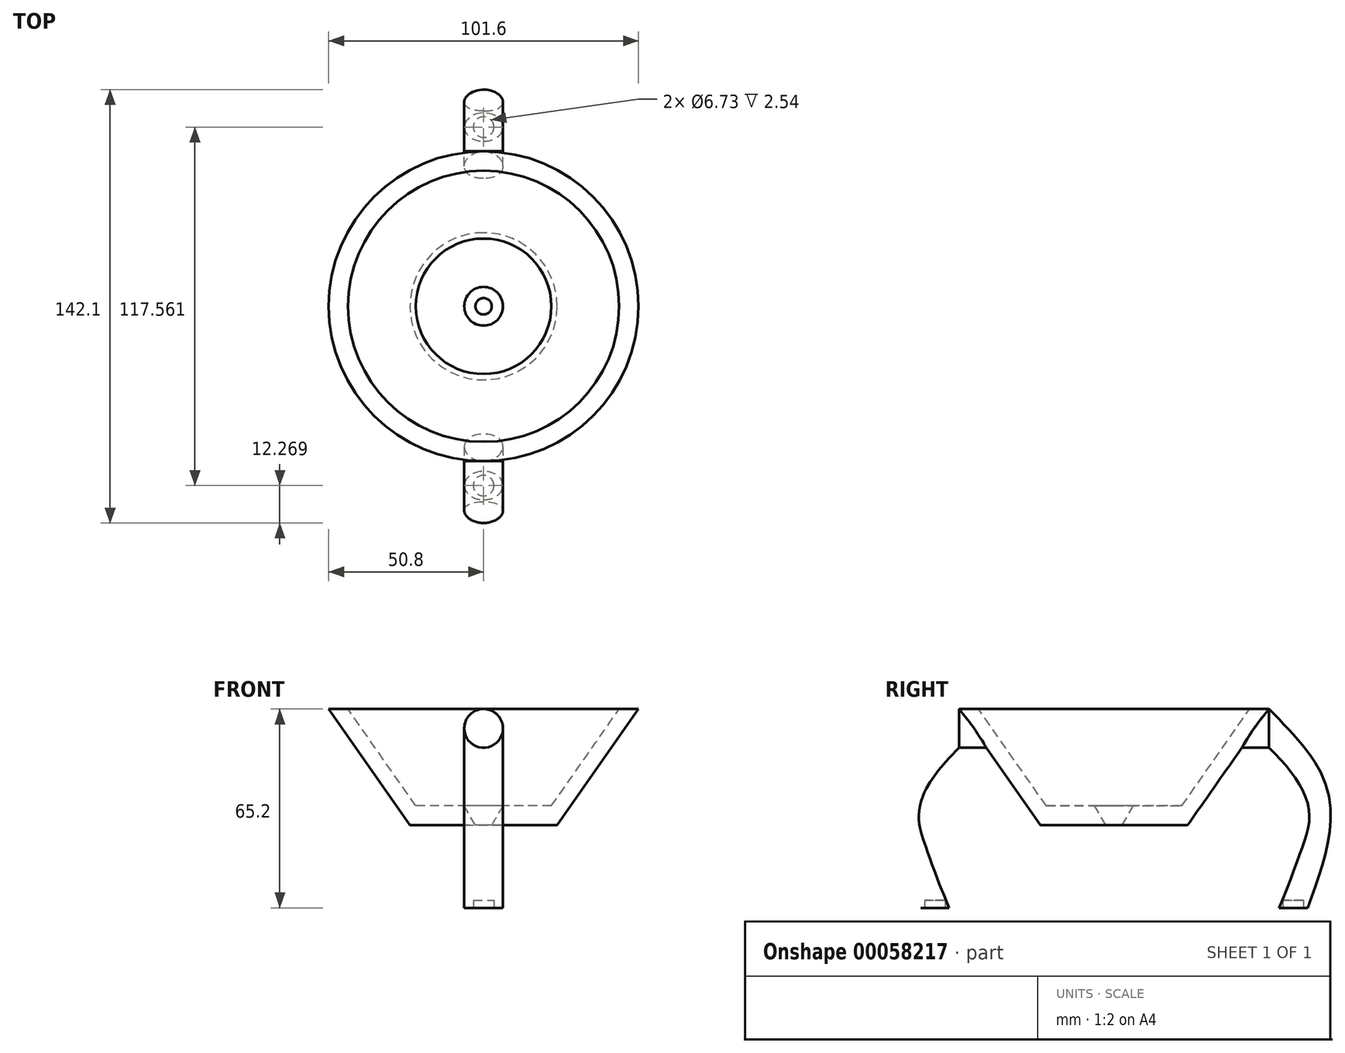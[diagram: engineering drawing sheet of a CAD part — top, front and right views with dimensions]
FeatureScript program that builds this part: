
annotation { "Feature Type Name" : "Feature", "Feature Type Description" : "" }
export const myFeature = defineFeature(function(context is Context, id is Id, definition is map)
    precondition{}
    {
        {
            var Q0;
            Q0=qCreatedBy(makeId("Top.planeOp"),FACE);
            var sketch = newSketch(context, id + "F0", { "sketchPlane" : qUnion([Q0])});
            skCircle(sketch, "E0", {"center": v(0, 0) * mm, "radius": 50.8 * mm});
            skSolve(sketch);
        }
        {
            var Q0;
            Q0 = qSketchRegion(id + "F0", true);
            extrude(context, id + "F1", {"entities" : qUnion([Q0]), "oppositeDirection" : true, "depth" : 38.1 * mm, "hasDraft" : true, "draftAngle" : 35 * degree, "draftPullDirection" : true});
        }
        {
            var Q0;
            Q0=makeQuery(id+"F1.opExtrude","CAP_FACE",FACE,{"disambiguationData":[OSD([sQuery(id+"F0.wireOp",EDGE,"E0")])],"isStart":true});
            var sketch = newSketch(context, id + "F2", { "sketchPlane" : qUnion([Q0])});
            skCircle(sketch, "E1", {"center": v(0, 0) * mm, "radius": 44.45 * mm});
            skSolve(sketch);
        }
        {
            var Q0;
            Q0 = qSketchRegion(id + "F2", true);
            extrude(context, id + "F3", {"entities" : qUnion([Q0]), "operationType" : NewBodyOperationType.REMOVE, "oppositeDirection" : true, "depth" : 31.75 * mm, "hasDraft" : true, "draftAngle" : 35 * degree, "draftPullDirection" : true});
        }
        {
            var Q0;
            Q0=qCreatedBy(makeId("Right.planeOp"),FACE);
            var sketch = newSketch(context, id + "F4", { "sketchPlane" : qUnion([Q0])});
            skPoint(sketch, "E2", {"position": v(-50.8, 0) * mm});
            skFitSpline(sketch, "E3", {"points": [v(-50.8, 0) * mm, v(-70.84, -31.02) * mm, v(-50.8, -97.59) * mm], "startDerivative": vector(-62.24, -64.04) * mm, "endDerivative": vector(44.05, -127.52) * mm});
            skFitSpline(sketch, "E4.MirrorCS", {"points": [v(50.8, 0) * mm, v(70.84, -31.02) * mm, v(50.8, -97.59) * mm], "startDerivative": vector(62.24, -64.04) * mm, "endDerivative": vector(-44.05, -127.52) * mm});
            skSolve(sketch);
        }
        {
            var Q0;
            Q0=sQuery(id+"F4.wireOp",VERTEX,"E2");
            var Q1;
            Q1=qCreatedBy(makeId("Front.planeOp"),FACE);
            cPlane(context, id + "F5", {"entities" : qUnion([Q0, Q1]), "cplaneType" : CPlaneType.PLANE_POINT, "offset" : 152.4 * mm, "width" : 152.4 * mm, "height" : 152.4 * mm});
        }
        {
            var Q0;
            Q0=qCreatedBy(id+"F5.planeOp",FACE);
            var sketch = newSketch(context, id + "F6", { "sketchPlane" : qUnion([Q0])});
            skCircle(sketch, "E5", {"center": v(0, -6.35) * mm, "radius": 6.35 * mm});
            skSolve(sketch);
        }
        {
            var Q0;
            Q0=makeQuery(id+"F6.imprint","IMPRINT",FACE,{"disambiguationData":[TD([[makeQuery(id+"F6.imprint","IMPRINT",EDGE,{"derivedFrom":sQuery(id+"F6.wireOp",EDGE,"E5")}),1.0]])]});
            var Q1;
            Q1=sQuery(id+"F4.wireOp",EDGE,"E3");
            sweep(context, id + "F7", {"profiles" : qUnion([Q0]), "path" : qUnion([Q1])});
        }
        {
            var Q0;
            Q0=makeQuery(id+"F6.imprint","IMPRINT",FACE,{"disambiguationData":[TD([[makeQuery(id+"F6.imprint","IMPRINT",EDGE,{"derivedFrom":sQuery(id+"F6.wireOp",EDGE,"E5")}),1.0]])]});
            var Q1;
            Q1=makeQuery(id+"F1.opExtrude","SWEPT_FACE",FACE,{"disambiguationData":[OSD([sQuery(id+"F0.wireOp",EDGE,"E0")])]});
            extrude(context, id + "F8", {"entities" : qUnion([Q0]), "endBound" : BoundingType.UP_TO_SURFACE, "oppositeDirection" : true, "endBoundEntityFace" : qUnion([Q1]), "depth" : 25.4 * mm});
        }
        {
            var Q0;
            Q0=makeQuery(id+"F7.opSweep","SWEPT_BODY",BODY,{"disambiguationData":[OSD([sQuery(id+"F4.wireOp",EDGE,"E3"),sQuery(id+"F6.wireOp",EDGE,"E5")])]});
            var Q1;
            Q1=makeQuery(id+"F8.opExtrude","SWEPT_BODY",BODY,{"disambiguationData":[OSD([sQuery(id+"F6.wireOp",EDGE,"E5")])]});
            var Q2;
            Q2=qCreatedBy(makeId("Front.planeOp"),FACE);
            mirror(context, id + "F9", {"operationType" : NewBodyOperationType.ADD, "entities" : qUnion([Q0, Q1]), "mirrorPlane" : qUnion([Q2])});
        }
        {
            var Q0;
            Q0=qCreatedBy(makeId("Right.planeOp"),FACE);
            var sketch = newSketch(context, id + "F10", { "sketchPlane" : qUnion([Q0])});
            skLineSegment(sketch, "E6", {"start": v(0, 0) * mm, "end": v(0, -8.97) * mm});
            skSolve(sketch);
        }
        {
            var Q0;
            Q0=makeQuery(id+"F7.opSweep","CAP_FACE",FACE,{"disambiguationData":[OSD([sQuery(id+"F4.wireOp",VERTEX,"E3.end"),sQuery(id+"F6.wireOp",EDGE,"E5")])],"isStart":false});
            var sketch = newSketch(context, id + "F11", { "sketchPlane" : qUnion([Q0])});
            skPoint(sketch, "E7", {"position": v(0, -11.28) * mm});
            skSolve(sketch);
        }
        {
            var Q0;
            Q0=sQuery(id+"F11.wireOp",VERTEX,"E7");
            var Q1;
            Q1=qCreatedBy(makeId("Top.planeOp"),FACE);
            cPlane(context, id + "F12", {"entities" : qUnion([Q0, Q1]), "cplaneType" : CPlaneType.PLANE_POINT, "offset" : 152.4 * mm, "width" : 152.4 * mm, "height" : 152.4 * mm});
        }
        {
            var Q0;
            Q0=qCreatedBy(id+"F12.planeOp",FACE);
            var sketch = newSketch(context, id + "F13", { "sketchPlane" : qUnion([Q0])});
            skLineSegment(sketch, "E8.bottom", {"start": v(-17.67, -100.3) * mm, "end": v(22.41, -100.3) * mm});
            skLineSegment(sketch, "E8.top", {"start": v(-17.67, 121.35) * mm, "end": v(22.41, 121.35) * mm});
            skLineSegment(sketch, "E8.left", {"start": v(-17.67, -100.3) * mm, "end": v(-17.67, 121.35) * mm});
            skLineSegment(sketch, "E8.right", {"start": v(22.41, -100.3) * mm, "end": v(22.41, 121.35) * mm});
            skSolve(sketch);
        }
        {
            var Q0;
            Q0 = qSketchRegion(id + "F13", true);
            extrude(context, id + "F14", {"entities" : qUnion([Q0]), "operationType" : NewBodyOperationType.REMOVE, "depth" : 38.1 * mm});
        }
        {
            var Q0;
            Q0=makeQuery(id+"F14.boolean.opBoolean","COPY",FACE,{"disambiguationData":[TD([makeQuery(id+"F7.opSweep","SWEPT_FACE",FACE,{"disambiguationData":[OSD([sQuery(id+"F4.wireOp",EDGE,"E3"),sQuery(id+"F6.wireOp",EDGE,"E5")])]})])],"derivedFrom":makeQuery(id+"F14.opExtrude","CAP_FACE",FACE,{"disambiguationData":[OSD([sQuery(id+"F13.wireOp",EDGE,"E8.bottom"),sQuery(id+"F13.wireOp",EDGE,"E8.top"),sQuery(id+"F13.wireOp",EDGE,"E8.left"),sQuery(id+"F13.wireOp",EDGE,"E8.right")])],"isStart":false})});
            var sketch = newSketch(context, id + "F15", { "sketchPlane" : qUnion([Q0])});
            skPoint(sketch, "E9", {"position": v(0, 63.44) * mm});
            skSolve(sketch);
        }
        {
            var Q0;
            Q0=makeQuery(id+"F14.boolean.opBoolean","COPY",FACE,{"disambiguationData":[TD([makeQuery(id+"F9.opPattern","COPY",FACE,{"derivedFrom":makeQuery(id+"F7.opSweep","SWEPT_FACE",FACE,{"disambiguationData":[OSD([sQuery(id+"F4.wireOp",EDGE,"E3"),sQuery(id+"F6.wireOp",EDGE,"E5")])]}),"instanceName":"1"})])],"derivedFrom":makeQuery(id+"F14.opExtrude","CAP_FACE",FACE,{"disambiguationData":[OSD([sQuery(id+"F13.wireOp",EDGE,"E8.bottom"),sQuery(id+"F13.wireOp",EDGE,"E8.top"),sQuery(id+"F13.wireOp",EDGE,"E8.left"),sQuery(id+"F13.wireOp",EDGE,"E8.right")])],"isStart":false})});
            var sketch = newSketch(context, id + "F16", { "sketchPlane" : qUnion([Q0])});
            skCircle(sketch, "E10", {"center": v(0, 0) * mm, "radius": 63.44 * mm});
            skSolve(sketch);
        }
        {
            var Q0;
            Q0 = qSketchRegion(id + "F16", true);
            extrude(context, id + "F17", {"entities" : qUnion([Q0]), "operationType" : NewBodyOperationType.ADD, "depth" : 6.35 * mm, "hasDraft" : true, "draftAngle" : 45 * degree, "draftPullDirection" : true});
        }
        {
            var Q0;
            Q0=makeQuery(id+"F17.opExtrude","CAP_FACE",FACE,{"disambiguationData":[OSD([sQuery(id+"F16.wireOp",EDGE,"E10")])],"isStart":true});
            var sketch = newSketch(context, id + "F18", { "sketchPlane" : qUnion([Q0])});
            skCircle(sketch, "E11", {"center": v(0, 0) * mm, "radius": 54.12 * mm});
            skSolve(sketch);
        }
        {
            var Q0;
            Q0 = qSketchRegion(id + "F18", true);
            extrude(context, id + "F19", {"entities" : qUnion([Q0]), "operationType" : NewBodyOperationType.REMOVE, "oppositeDirection" : true, "depth" : 3.17 * mm, "hasDraft" : true, "draftAngle" : 45 * degree, "draftPullDirection" : true});
        }
        {
            var Q0;
            Q0=makeQuery(id+"F3.boolean.opBoolean","COPY",FACE,{"derivedFrom":makeQuery(id+"F3.opExtrude","CAP_FACE",FACE,{"disambiguationData":[OSD([sQuery(id+"F2.wireOp",EDGE,"E1")])],"isStart":false})});
            var sketch = newSketch(context, id + "F20", { "sketchPlane" : qUnion([Q0])});
            skCircle(sketch, "E12", {"center": v(0, 0) * mm, "radius": 6.35 * mm});
            skSolve(sketch);
        }
        {
            var Q0;
            Q0 = qSketchRegion(id + "F20", true);
            extrude(context, id + "F21", {"entities" : qUnion([Q0]), "operationType" : NewBodyOperationType.REMOVE, "endBound" : BoundingType.UP_TO_NEXT, "oppositeDirection" : true, "depth" : 25.4 * mm, "hasDraft" : true, "draftAngle" : 30 * degree, "draftPullDirection" : true});
        }
        {
            var Q0;
            Q0=makeQuery(id+"F19.boolean.opBoolean","SPLIT",FACE,{"disambiguationData":[OD(1.0)],"derivedFrom":makeQuery(id+"F17.opExtrude","CAP_FACE",FACE,{"disambiguationData":[OSD([sQuery(id+"F16.wireOp",EDGE,"E10")])],"isStart":true})});
            var sketch = newSketch(context, id + "F22", { "sketchPlane" : qUnion([Q0])});
            skLineSegment(sketch, "E13.rect.bottom", {"start": v(-110.33, 93.04) * mm, "end": v(110.33, 93.04) * mm});
            skLineSegment(sketch, "E13.rect.top", {"start": v(-110.33, -93.04) * mm, "end": v(110.33, -93.04) * mm});
            skLineSegment(sketch, "E13.rect.left", {"start": v(-110.33, 93.04) * mm, "end": v(-110.33, -93.04) * mm});
            skLineSegment(sketch, "E13.rect.right", {"start": v(110.33, 93.04) * mm, "end": v(110.33, -93.04) * mm});
            skPoint(sketch, "E13.rect.middle", {"position": v(0, 0) * mm});
            skSolve(sketch);
        }
        {
            var Q0;
            Q0 = qSketchRegion(id + "F22", true);
            extrude(context, id + "F23", {"entities" : qUnion([Q0]), "operationType" : NewBodyOperationType.REMOVE, "oppositeDirection" : true, "depth" : 25.4 * mm});
        }
        {
            var Q0;
            Q0=makeQuery(id+"F23.boolean.opBoolean","COPY",FACE,{"disambiguationData":[TD([makeQuery(id+"F9.opPattern","COPY",FACE,{"derivedFrom":makeQuery(id+"F7.opSweep","SWEPT_FACE",FACE,{"disambiguationData":[OSD([sQuery(id+"F4.wireOp",EDGE,"E3"),sQuery(id+"F6.wireOp",EDGE,"E5")])]}),"instanceName":"1"})])],"derivedFrom":makeQuery(id+"F23.opExtrude","CAP_FACE",FACE,{"disambiguationData":[OSD([sQuery(id+"F22.wireOp",EDGE,"E13.rect.bottom"),sQuery(id+"F22.wireOp",EDGE,"E13.rect.top"),sQuery(id+"F22.wireOp",EDGE,"E13.rect.left"),sQuery(id+"F22.wireOp",EDGE,"E13.rect.right")])],"isStart":true})});
            var sketch = newSketch(context, id + "F24", { "sketchPlane" : qUnion([Q0])});
            skCircle(sketch, "E14", {"center": v(0, 58.78) * mm, "radius": 3.37 * mm});
            skCircle(sketch, "E15.MirrorC", {"center": v(0, -58.78) * mm, "radius": 3.37 * mm});
            skSolve(sketch);
        }
        {
            var Q0;
            Q0 = qSketchRegion(id + "F24", true);
            extrude(context, id + "F25", {"entities" : qUnion([Q0]), "operationType" : NewBodyOperationType.REMOVE, "oppositeDirection" : true, "depth" : 2.54 * mm});
        }
    });
